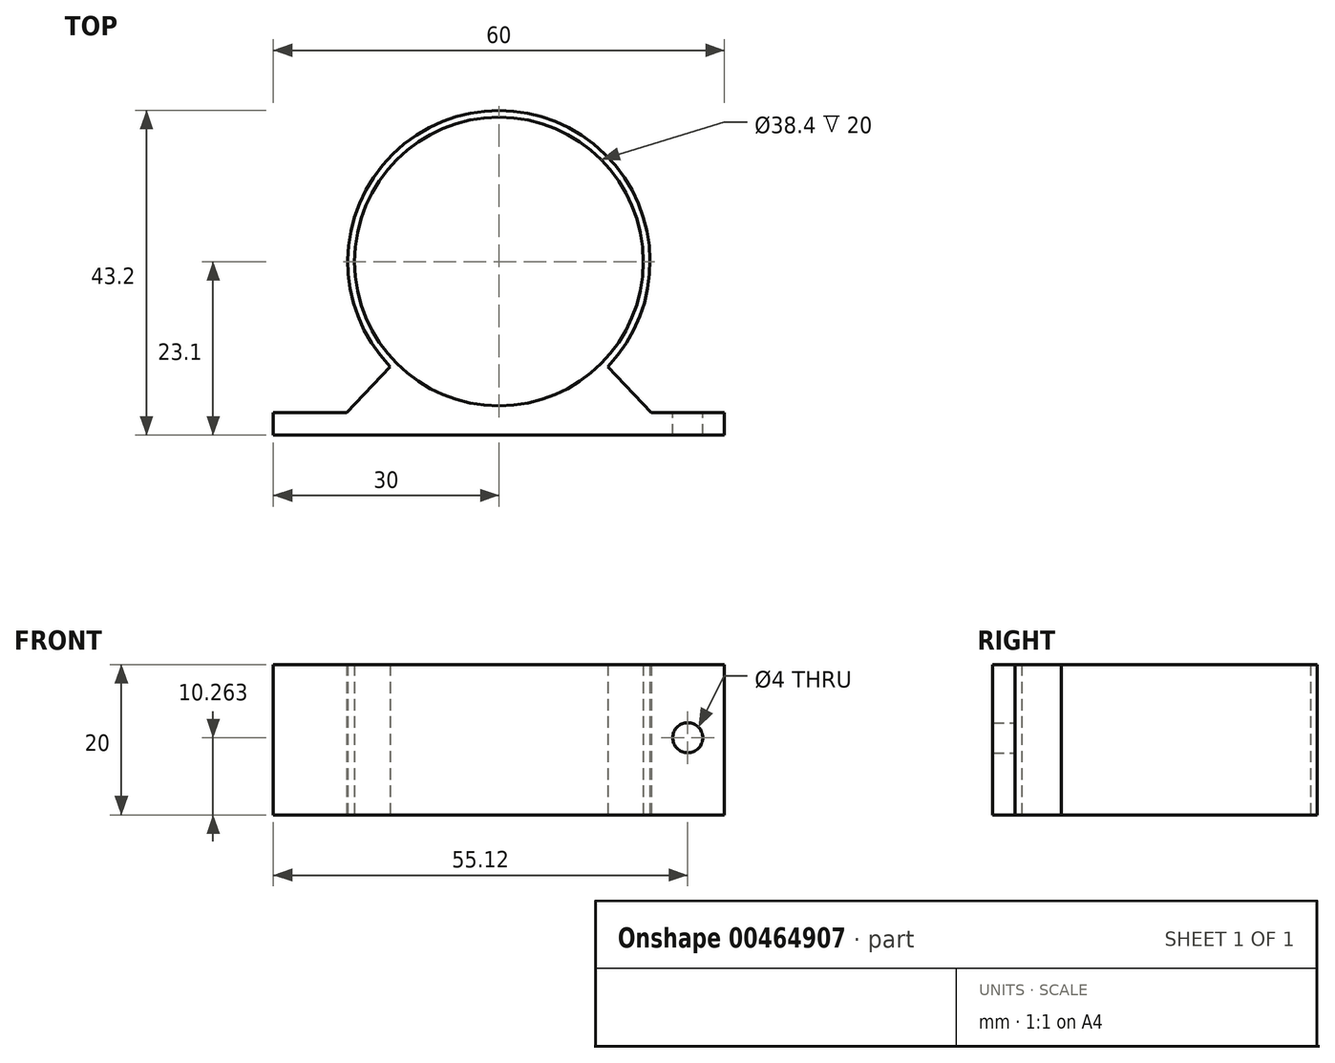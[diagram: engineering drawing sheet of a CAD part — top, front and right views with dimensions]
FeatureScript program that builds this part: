
annotation { "Feature Type Name" : "Feature", "Feature Type Description" : "" }
export const myFeature = defineFeature(function(context is Context, id is Id, definition is map)
    precondition{}
    {
        {
            var Q0;
            Q0=qCreatedBy(makeId("Top.planeOp"),FACE);
            var sketch = newSketch(context, id + "F0", { "sketchPlane" : qUnion([Q0])});
            skCircle(sketch, "E0", {"center": v(0, 0) * mm, "radius": 19.2 * mm});
            skCircle(sketch, "E1", {"center": v(0, 0) * mm, "radius": 20.1 * mm});
            skLineSegment(sketch, "E2.bottom", {"start": v(0, -20.1) * mm, "end": v(30, -20.1) * mm});
            skLineSegment(sketch, "E2.top", {"start": v(0, -23.1) * mm, "end": v(30, -23.1) * mm});
            skLineSegment(sketch, "E2.left", {"start": v(0, -20.1) * mm, "end": v(0, -23.1) * mm});
            skLineSegment(sketch, "E2.right", {"start": v(30, -20.1) * mm, "end": v(30, -23.1) * mm});
            skLineSegment(sketch, "E3.MirrorCS", {"start": v(0, -23.1) * mm, "end": v(-30, -23.1) * mm});
            skLineSegment(sketch, "E4.MirrorCS", {"start": v(0, -20.1) * mm, "end": v(-30, -20.1) * mm});
            skLineSegment(sketch, "E5.MirrorCS", {"start": v(-30, -20.1) * mm, "end": v(-30, -23.1) * mm});
            skLineSegment(sketch, "E6", {"start": v(-14.46, -13.96) * mm, "end": v(-20.24, -20.1) * mm});
            skLineSegment(sketch, "E7.MirrorCS", {"start": v(14.46, -13.96) * mm, "end": v(20.24, -20.1) * mm});
            skSolve(sketch);
        }
        {
            var Q0;
            Q0=makeQuery(id+"F0.imprint","IMPRINT",FACE,{"disambiguationData":[TD([[makeQuery(id+"F0.imprint","IMPRINT",EDGE,{"derivedFrom":sQuery(id+"F0.wireOp",EDGE,"E0")}),-1.0]])]});
            var Q1;
            {var subQ3=sQuery(id+"F0.wireOp",EDGE,"E2.left");Q1=makeQuery(id+"F0.imprint","IMPRINT",FACE,{"disambiguationData":[TD([[makeQuery(id+"F0.imprint","IMPRINT",EDGE,{"derivedFrom":subQ3}),-1.0]])]});}
            var Q2;
            {var subQ3=sQuery(id+"F0.wireOp",EDGE,"E7.MirrorCS");Q2=makeQuery(id+"F0.imprint","IMPRINT",FACE,{"disambiguationData":[TD([[makeQuery(id+"F0.imprint","IMPRINT",EDGE,{"derivedFrom":subQ3}),-1.0]])]});}
            var Q3;
            {var subQ3=sQuery(id+"F0.wireOp",EDGE,"E6");Q3=makeQuery(id+"F0.imprint","IMPRINT",FACE,{"disambiguationData":[TD([[makeQuery(id+"F0.imprint","IMPRINT",EDGE,{"derivedFrom":subQ3}),1.0]])]});}
            var Q4;
            Q4=makeQuery(id+"F0.imprint","IMPRINT",FACE,{"disambiguationData":[TD([[makeQuery(id+"F0.imprint","IMPRINT",EDGE,{"derivedFrom":sQuery(id+"F0.wireOp",EDGE,"E2.top")}),1.0]])]});
            extrude(context, id + "F1", {"entities" : qUnion([Q0, Q1, Q2, Q3, Q4]), "depth" : 20 * mm});
        }
        {
            var Q0;
            Q0=makeQuery(id+"F1.opExtrude","SWEPT_FACE",FACE,{"disambiguationData":[OSD([sQuery(id+"F0.wireOp",EDGE,"E2.bottom")])]});
            var sketch = newSketch(context, id + "F2", { "sketchPlane" : qUnion([Q0])});
            skPoint(sketch, "E8.oppositeSnap0", {"position": v(-25.12, 0) * mm});
            skLineSegment(sketch, "E8.bottom", {"start": v(-30, 0) * mm, "end": v(-25.12, 0) * mm});
            skLineSegment(sketch, "E8.top", {"start": v(-30, 10.26) * mm, "end": v(-25.12, 10.26) * mm});
            skLineSegment(sketch, "E8.left", {"start": v(-30, 0) * mm, "end": v(-30, 10.26) * mm});
            skLineSegment(sketch, "E8.right", {"start": v(-25.12, 0) * mm, "end": v(-25.12, 10.26) * mm});
            skCircle(sketch, "E9", {"center": v(-25.12, 10.26) * mm, "radius": 2 * mm});
            skCircle(sketch, "E10.MirrorC", {"center": v(25.12, 10.26) * mm, "radius": 2 * mm});
            skSolve(sketch);
        }
        {
            var Q0;
            {var subQ0=sQuery(id+"F2.wireOp",EDGE,"E8.right");var subQ1=sQuery(id+"F2.wireOp",EDGE,"E8.top");var subQ2=makeQuery(id+"F2.imprint","INTERSECT",VERTEX,{"derivedFrom":[subQ1,subQ0]});Q0=makeQuery(id+"F2.imprint","IMPRINT",FACE,{"disambiguationData":[TD([[makeQuery(id+"F2.imprint","IMPRINT",EDGE,{"disambiguationData":[TD([[subQ2,1.0]])],"derivedFrom":subQ1}),1.0]])]});}
            var Q1;
            {var subQ0=sQuery(id+"F2.wireOp",EDGE,"E8.right");var subQ1=sQuery(id+"F2.wireOp",EDGE,"E8.top");var subQ2=makeQuery(id+"F2.imprint","INTERSECT",VERTEX,{"derivedFrom":[subQ1,subQ0]});Q1=makeQuery(id+"F2.imprint","IMPRINT",FACE,{"disambiguationData":[TD([[makeQuery(id+"F2.imprint","IMPRINT",EDGE,{"disambiguationData":[TD([[subQ2,1.0]])],"derivedFrom":subQ1}),-1.0]])]});}
            var Q2;
            Q2=makeQuery(id+"F2.imprint","IMPRINT",FACE,{"disambiguationData":[TD([[makeQuery(id+"F2.imprint","IMPRINT",EDGE,{"derivedFrom":sQuery(id+"F2.wireOp",EDGE,"E10.MirrorC")}),-1.0]])]});
            extrude(context, id + "F3", {"entities" : qUnion([Q0, Q1, Q2]), "operationType" : NewBodyOperationType.REMOVE, "oppositeDirection" : true, "depth" : 25 * mm});
        }
    });
